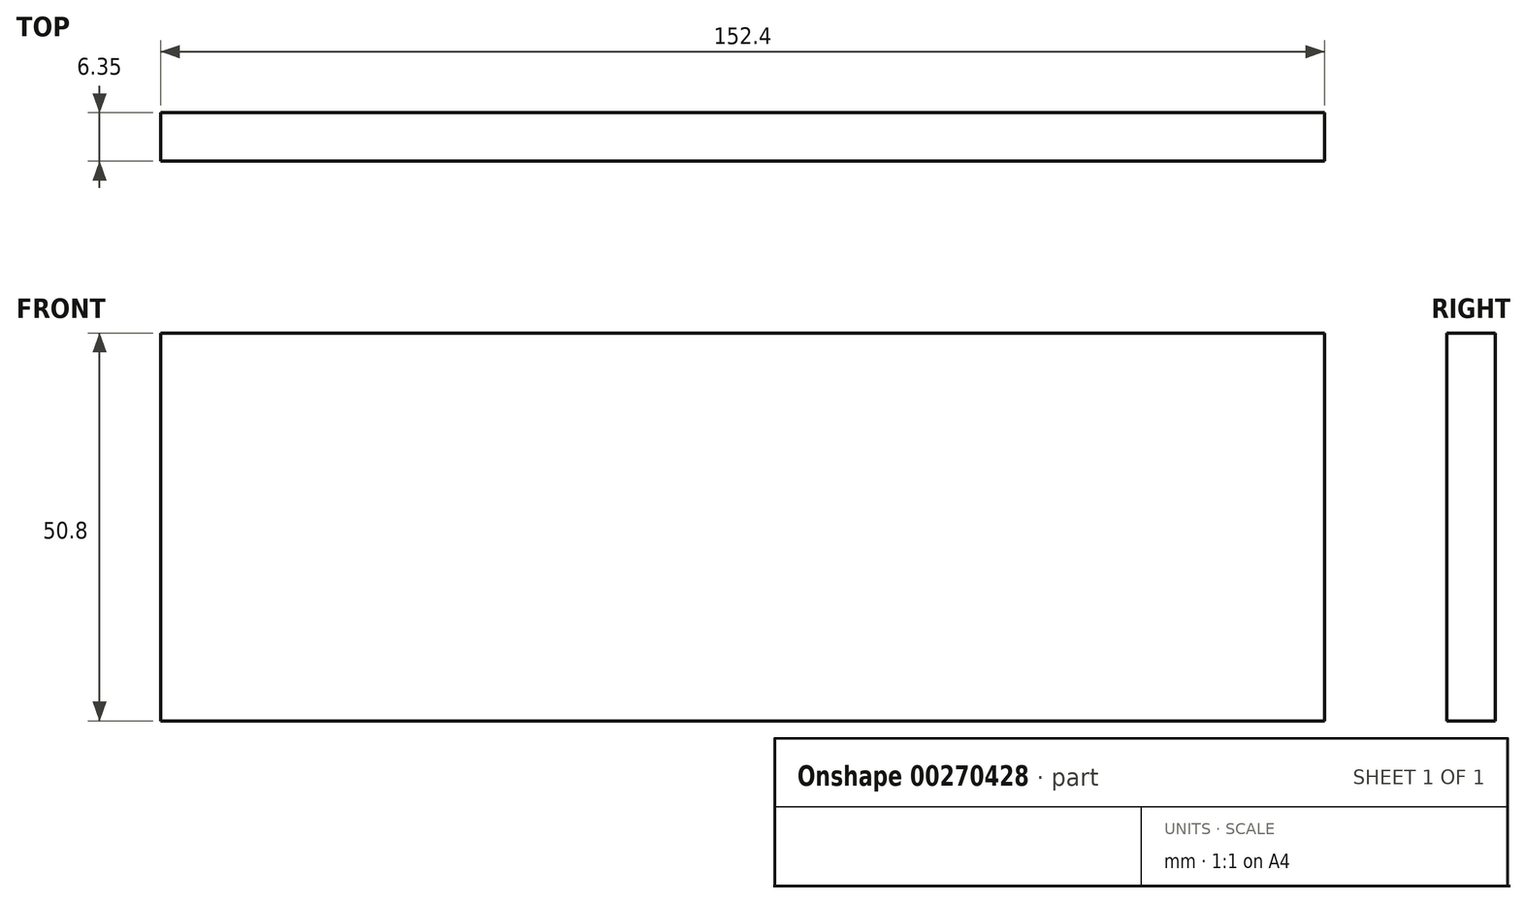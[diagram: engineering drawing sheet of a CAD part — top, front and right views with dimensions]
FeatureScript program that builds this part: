
annotation { "Feature Type Name" : "Feature", "Feature Type Description" : "" }
export const myFeature = defineFeature(function(context is Context, id is Id, definition is map)
    precondition{}
    {
        {
            var Q0;
            Q0=qCreatedBy(makeId("Front.planeOp"),FACE);
            var sketch = newSketch(context, id + "F0", { "sketchPlane" : qUnion([Q0])});
            skLineSegment(sketch, "E0.bottom", {"start": v(76.2, 25.4) * mm, "end": v(-76.2, 25.4) * mm});
            skLineSegment(sketch, "E0.top", {"start": v(76.2, -25.4) * mm, "end": v(-76.2, -25.4) * mm});
            skLineSegment(sketch, "E0.left", {"start": v(76.2, 25.4) * mm, "end": v(76.2, -25.4) * mm});
            skLineSegment(sketch, "E0.right", {"start": v(-76.2, 25.4) * mm, "end": v(-76.2, -25.4) * mm});
            skPoint(sketch, "E0.middle", {"position": v(0, 0) * mm});
            skLineSegment(sketch, "E1", {"start": v(1.3, 0) * mm, "end": v(-38.1, 0) * mm});
            skLineSegment(sketch, "E2", {"start": v(-38.1, 0) * mm, "end": v(0, 0) * mm});
            skLineSegment(sketch, "E3", {"start": v(0, 0) * mm, "end": v(38.1, 0) * mm});
            skSolve(sketch);
        }
        {
            var Q0;
            Q0=makeQuery(id+"F0.imprint","IMPRINT",FACE,{"disambiguationData":[TD([[makeQuery(id+"F0.imprint","IMPRINT",EDGE,{"derivedFrom":sQuery(id+"F0.wireOp",EDGE,"E0.bottom")}),1.0]])]});
            extrude(context, id + "F1", {"entities" : qUnion([Q0]), "depth" : 6.35 * mm});
        }
    });
